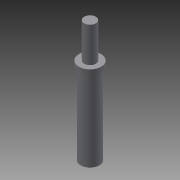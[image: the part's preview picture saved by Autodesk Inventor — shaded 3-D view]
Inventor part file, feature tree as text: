
AUTODESK INVENTOR PART (.ipt)
format: ipt  version: 2014 (Build 180170000, 170)  size: 87,040 bytes
history: native  units: mm
features: sketch x2, revolve x1, extrude x1
ambient origin geometry x8: Origin, YZ Plane, XZ Plane, XY Plane, X Axis, Y Axis, Z Axis, Center Point
bodies: Solid1 (feature_tree)
feature tree (4):
  revolve  "Revolution1"  [1 undecoded]
  extrude  "Extrusion1"  Depth=2.0mm
  sketch  "Sketch1"  dims[d0=4.0mm d1=4.75mm]
  sketch  "Sketch2"  dims[d2=35.0mm d3=2.0mm d4=15.0mm d5=2.5mm d6=90.0deg d10=10.0mm d11=0.0mm d12=7.9375mm]
note: 1 required parameter value undecoded (feature->parameter linkage not recoverable at this tier; creation-order binding heuristic only, values carry confidence <= 0.55)
